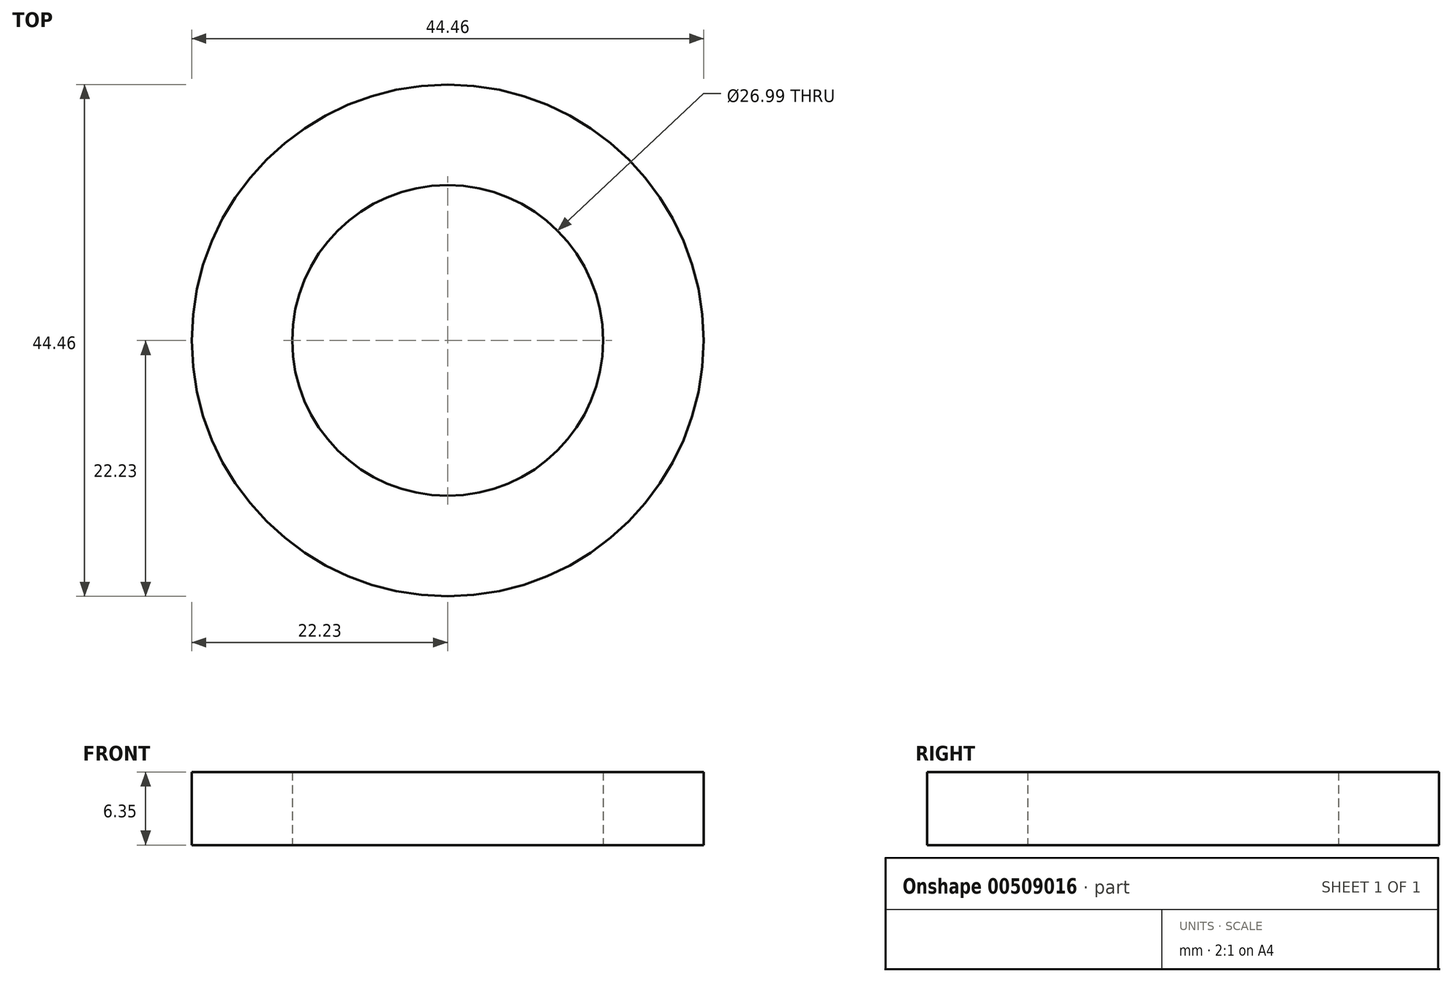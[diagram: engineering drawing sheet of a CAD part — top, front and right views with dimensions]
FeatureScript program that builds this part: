
annotation { "Feature Type Name" : "Feature", "Feature Type Description" : "" }
export const myFeature = defineFeature(function(context is Context, id is Id, definition is map)
    precondition{}
    {
        {
            var Q0;
            Q0=qCreatedBy(makeId("Top.planeOp"),FACE);
            var sketch = newSketch(context, id + "F0", { "sketchPlane" : qUnion([Q0])});
            skCircle(sketch, "E0", {"center": v(0, 0) * mm, "radius": 13.5 * mm});
            skCircle(sketch, "E1", {"center": v(0, 0) * mm, "radius": 22.23 * mm});
            skSolve(sketch);
        }
        {
            var Q0;
            Q0=makeQuery(id+"F0.imprint","IMPRINT",FACE,{"disambiguationData":[TD([[makeQuery(id+"F0.imprint","IMPRINT",EDGE,{"derivedFrom":sQuery(id+"F0.wireOp",EDGE,"E0")}),-1.0]])]});
            extrude(context, id + "F1", {"entities" : qUnion([Q0]), "depth" : 6.35 * mm, "offsetDistance" : 25.4 * mm});
        }
    });
